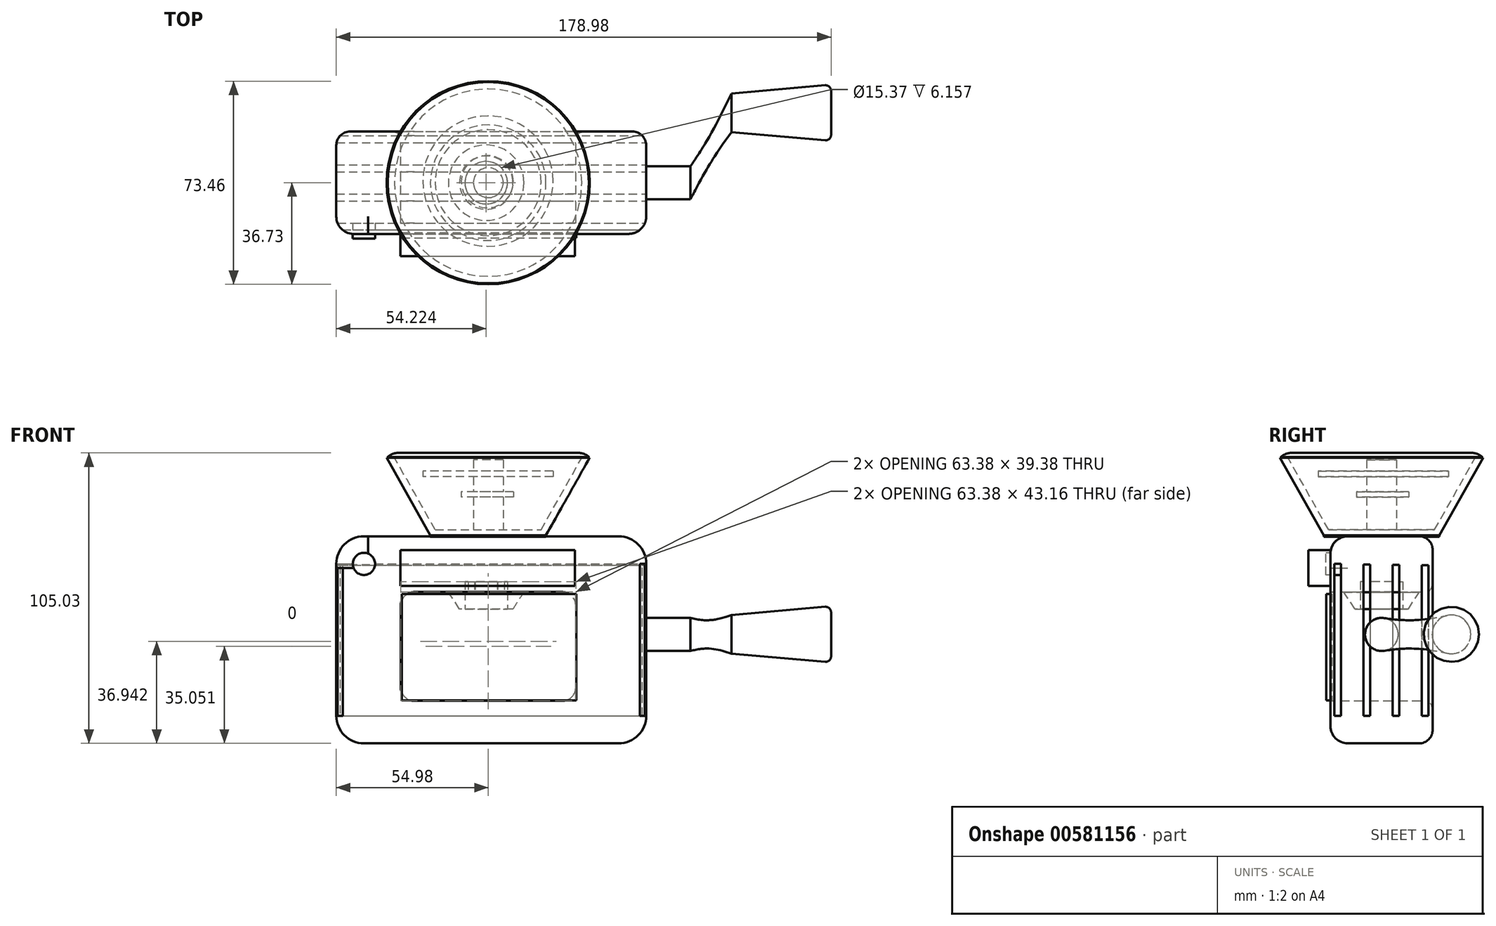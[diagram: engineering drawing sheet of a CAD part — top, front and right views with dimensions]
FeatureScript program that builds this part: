
annotation { "Feature Type Name" : "Feature", "Feature Type Description" : "" }
export const myFeature = defineFeature(function(context is Context, id is Id, definition is map)
    precondition{}
    {
        {
            var Q0;
            Q0=qCreatedBy(makeId("Front.planeOp"),FACE);
            var sketch = newSketch(context, id + "F0", { "sketchPlane" : qUnion([Q0])});
            skLineSegment(sketch, "E0.bottom", {"start": v(-54.98, 43.58) * mm, "end": v(57.14, 43.58) * mm});
            skLineSegment(sketch, "E0.top", {"start": v(-54.98, -31.33) * mm, "end": v(57.14, -31.33) * mm});
            skLineSegment(sketch, "E0.left", {"start": v(-54.98, 43.58) * mm, "end": v(-54.98, -31.33) * mm});
            skLineSegment(sketch, "E0.right", {"start": v(57.14, 43.58) * mm, "end": v(57.14, -31.33) * mm});
            skSolve(sketch);
        }
        {
            var Q0;
            Q0=makeQuery(id+"F0.imprint","IMPRINT",FACE,{"disambiguationData":[TD([[makeQuery(id+"F0.imprint","IMPRINT",EDGE,{"derivedFrom":sQuery(id+"F0.wireOp",EDGE,"E0.bottom")}),-1.0]])]});
            var sketch = newSketch(context, id + "F1", { "sketchPlane" : qUnion([Q0])});
            skLineSegment(sketch, "E1.bottom", {"start": v(-31.7, 23.4) * mm, "end": v(31.7, 23.4) * mm});
            skLineSegment(sketch, "E1.top", {"start": v(-31.7, -15.97) * mm, "end": v(31.7, -15.97) * mm});
            skLineSegment(sketch, "E1.left", {"start": v(-31.7, 23.4) * mm, "end": v(-31.7, -15.97) * mm});
            skLineSegment(sketch, "E1.right", {"start": v(31.7, 23.4) * mm, "end": v(31.7, -15.97) * mm});
            skSolve(sketch);
        }
        {
            var Q0;
            Q0=makeQuery(id+"F1.imprint","IMPRINT",FACE,{"disambiguationData":[TD([[makeQuery(id+"F1.imprint","IMPRINT",EDGE,{"derivedFrom":sQuery(id+"F1.wireOp",EDGE,"E1.bottom")}),1.0]])]});
            var sketch = newSketch(context, id + "F2", { "sketchPlane" : qUnion([Q0])});
            skSolve(sketch);
        }
        {
            var Q0;
            Q0 = qSketchRegion(id + "F2", true);
            var Q1;
            Q1=makeQuery(id+"F1.imprint","IMPRINT",FACE,{"disambiguationData":[TD([[makeQuery(id+"F1.imprint","IMPRINT",EDGE,{"derivedFrom":sQuery(id+"F1.wireOp",EDGE,"E1.bottom")}),1.0]])]});
            extrude(context, id + "F3", {"entities" : qUnion([Q0, Q1]), "endBound" : BoundingType.SYMMETRIC, "depth" : 37 * mm, "offsetDistance" : 25 * mm});
        }
        {
            var Q0;
            Q0=makeQuery(id+"F3.opExtrude","SWEPT_EDGE",EDGE,{"disambiguationData":[OSD([sQuery(id+"F0.wireOp",EDGE,"E0.bottom"),sQuery(id+"F0.wireOp",EDGE,"E0.right")])]});
            var Q1;
            Q1=makeQuery(id+"F3.opExtrude","SWEPT_EDGE",EDGE,{"disambiguationData":[OSD([sQuery(id+"F0.wireOp",EDGE,"E0.bottom"),sQuery(id+"F0.wireOp",EDGE,"E0.left")])]});
            var Q2;
            Q2=makeQuery(id+"F3.opExtrude","SWEPT_EDGE",EDGE,{"disambiguationData":[OSD([sQuery(id+"F0.wireOp",EDGE,"E0.top"),sQuery(id+"F0.wireOp",EDGE,"E0.right")])]});
            var Q3;
            Q3=makeQuery(id+"F3.opExtrude","SWEPT_EDGE",EDGE,{"disambiguationData":[OSD([sQuery(id+"F0.wireOp",EDGE,"E0.top"),sQuery(id+"F0.wireOp",EDGE,"E0.left")])]});
            fillet(context, id + "F4", {"entities" : qUnion([Q0, Q1, Q2, Q3]), "radius" : 10 * mm, "tangentPropagation" : true, "allowEdgeOverflow" : false});
        }
        {
            var Q0;
            Q0=makeQuery(id+"F3.opExtrude","SWEPT_EDGE",EDGE,{"disambiguationData":[OSD([sQuery(id+"F1.wireOp",EDGE,"E1.top"),sQuery(id+"F1.wireOp",EDGE,"E1.right")])]});
            var Q1;
            Q1=makeQuery(id+"F3.opExtrude","SWEPT_EDGE",EDGE,{"disambiguationData":[OSD([sQuery(id+"F1.wireOp",EDGE,"E1.bottom"),sQuery(id+"F1.wireOp",EDGE,"E1.right")])]});
            var Q2;
            Q2=makeQuery(id+"F3.opExtrude","SWEPT_EDGE",EDGE,{"disambiguationData":[OSD([sQuery(id+"F1.wireOp",EDGE,"E1.bottom"),sQuery(id+"F1.wireOp",EDGE,"E1.left")])]});
            var Q3;
            Q3=makeQuery(id+"F3.opExtrude","SWEPT_EDGE",EDGE,{"disambiguationData":[OSD([sQuery(id+"F1.wireOp",EDGE,"E1.top"),sQuery(id+"F1.wireOp",EDGE,"E1.left")])]});
            fillet(context, id + "F5", {"entities" : qUnion([Q0, Q1, Q2, Q3]), "radius" : 5 * mm, "tangentPropagation" : true, "allowEdgeOverflow" : false});
        }
        {
            var Q0;
            Q0=makeQuery(id+"F3.opExtrude","SWEPT_FACE",FACE,{"disambiguationData":[OSD([sQuery(id+"F0.wireOp",EDGE,"E0.right")])]});
            var sketch = newSketch(context, id + "F6", { "sketchPlane" : qUnion([Q0])});
            skLineSegment(sketch, "E2.bottom", {"start": v(-17.1, 33.58) * mm, "end": v(-14.63, 33.58) * mm});
            skLineSegment(sketch, "E2.top", {"start": v(-17.1, -21.33) * mm, "end": v(-14.63, -21.33) * mm});
            skLineSegment(sketch, "E2.left", {"start": v(-17.1, 33.58) * mm, "end": v(-17.1, -21.33) * mm});
            skLineSegment(sketch, "E2.right", {"start": v(-14.63, 33.58) * mm, "end": v(-14.63, -21.33) * mm});
            skLineSegment(sketch, "E3.1.0.0", {"start": v(-4.1, 33.4) * mm, "end": v(-4.1, -21.5) * mm});
            skLineSegment(sketch, "E3.1.0.1", {"start": v(-6.57, 33.4) * mm, "end": v(-4.1, 33.4) * mm});
            skLineSegment(sketch, "E3.1.0.2", {"start": v(-6.57, -21.5) * mm, "end": v(-4.1, -21.5) * mm});
            skLineSegment(sketch, "E3.1.0.3", {"start": v(-6.57, 33.4) * mm, "end": v(-6.57, -21.5) * mm});
            skLineSegment(sketch, "E3.2.0.0", {"start": v(6.43, 33.24) * mm, "end": v(6.43, -21.67) * mm});
            skLineSegment(sketch, "E3.2.0.1", {"start": v(3.97, 33.24) * mm, "end": v(6.43, 33.24) * mm});
            skLineSegment(sketch, "E3.2.0.2", {"start": v(3.97, -21.67) * mm, "end": v(6.43, -21.67) * mm});
            skLineSegment(sketch, "E3.2.0.3", {"start": v(3.97, 33.24) * mm, "end": v(3.97, -21.67) * mm});
            skLineSegment(sketch, "E3.3.0.0", {"start": v(16.96, 33.07) * mm, "end": v(16.96, -21.84) * mm});
            skLineSegment(sketch, "E3.3.0.1", {"start": v(14.5, 33.07) * mm, "end": v(16.96, 33.07) * mm});
            skLineSegment(sketch, "E3.3.0.2", {"start": v(14.5, -21.84) * mm, "end": v(16.96, -21.84) * mm});
            skLineSegment(sketch, "E3.3.0.3", {"start": v(14.5, 33.07) * mm, "end": v(14.5, -21.84) * mm});
            skLineSegment(sketch, "E3.direction1", {"start": v(-14.63, -21.33) * mm, "end": v(-4.1, -21.5) * mm, "construction": true});
            skSolve(sketch);
        }
        {
            var Q0;
            Q0=makeQuery(id+"F6.imprint","IMPRINT",FACE,{"disambiguationData":[TD([[makeQuery(id+"F6.imprint","IMPRINT",EDGE,{"derivedFrom":sQuery(id+"F6.wireOp",EDGE,"E2.bottom")}),1.0]])]});
            var Q1;
            {var subQ0=sQuery(id+"F6.wireOp",EDGE,"E3.1.0.1");Q1=makeQuery(id+"F6.imprint","IMPRINT",FACE,{"disambiguationData":[TD([[makeQuery(id+"F6.imprint","IMPRINT",EDGE,{"derivedFrom":subQ0}),-1.0]])]});}
            var Q2;
            {var subQ0=sQuery(id+"F6.wireOp",EDGE,"E3.2.0.1");Q2=makeQuery(id+"F6.imprint","IMPRINT",FACE,{"disambiguationData":[TD([[makeQuery(id+"F6.imprint","IMPRINT",EDGE,{"derivedFrom":subQ0}),-1.0]])]});}
            var Q3;
            {var subQ0=sQuery(id+"F6.wireOp",EDGE,"E3.3.0.1");Q3=makeQuery(id+"F6.imprint","IMPRINT",FACE,{"disambiguationData":[TD([[makeQuery(id+"F6.imprint","IMPRINT",EDGE,{"derivedFrom":subQ0}),-1.0]])]});}
            extrude(context, id + "F7", {"entities" : qUnion([Q0, Q1, Q2, Q3]), "operationType" : NewBodyOperationType.REMOVE, "oppositeDirection" : true, "depth" : 120 * mm, "offsetDistance" : 25 * mm});
        }
        {
            var Q0;
            {var subQ2=sQuery(id+"F0.wireOp",EDGE,"E0.right");var subQ7=makeQuery(id+"F3.opExtrude","SWEPT_FACE",FACE,{"disambiguationData":[OSD([subQ2])]});Q0=makeQuery(id+"F7.boolean.opBoolean","SPLIT",FACE,{"disambiguationData":[TD([makeQuery(id+"F7.opExtrude","SWEPT_FACE",FACE,{"disambiguationData":[OSD([sQuery(id+"F6.wireOp",EDGE,"E2.right")])]})])],"derivedFrom":subQ7});}
            var sketch = newSketch(context, id + "F8", { "sketchPlane" : qUnion([Q0])});
            skCircle(sketch, "E4", {"center": v(0, 8.07) * mm, "radius": 6 * mm});
            skSolve(sketch);
        }
        {
            var Q0;
            {var subQ0=sQuery(id+"F8.wireOp",EDGE,"E4");var subQ1=makeQuery(id+"F7.boolean.opBoolean","COPY",EDGE,{"derivedFrom":makeQuery(id+"F7.opExtrude","CAP_EDGE",EDGE,{"disambiguationData":[OSD([sQuery(id+"F6.wireOp",EDGE,"E3.2.0.3")])],"isStart":true})});var subQ2=makeQuery(id+"F8.imprint","INTERSECT",VERTEX,{"disambiguationData":[OD(0.0)],"derivedFrom":[subQ1,subQ0]});Q0=makeQuery(id+"F8.imprint","IMPRINT",FACE,{"disambiguationData":[TD([[makeQuery(id+"F8.imprint","IMPRINT",EDGE,{"disambiguationData":[TD([[subQ2,1.0]])],"derivedFrom":subQ0}),1.0]])]});}
            var Q1;
            {var subQ0=sQuery(id+"F8.wireOp",EDGE,"E4");var subQ1=makeQuery(id+"F7.boolean.opBoolean","COPY",EDGE,{"derivedFrom":makeQuery(id+"F7.opExtrude","CAP_EDGE",EDGE,{"disambiguationData":[OSD([sQuery(id+"F6.wireOp",EDGE,"E3.1.0.0")])],"isStart":true})});var subQ2=makeQuery(id+"F8.imprint","INTERSECT",VERTEX,{"disambiguationData":[OD(0.0)],"derivedFrom":[subQ1,subQ0]});Q1=makeQuery(id+"F8.imprint","IMPRINT",FACE,{"disambiguationData":[TD([[makeQuery(id+"F8.imprint","IMPRINT",EDGE,{"disambiguationData":[TD([[subQ2,1.0]])],"derivedFrom":subQ0}),1.0]])]});}
            var Q2;
            {var subQ0=sQuery(id+"F8.wireOp",EDGE,"E4");var subQ1=makeQuery(id+"F7.boolean.opBoolean","COPY",EDGE,{"derivedFrom":makeQuery(id+"F7.opExtrude","CAP_EDGE",EDGE,{"disambiguationData":[OSD([sQuery(id+"F6.wireOp",EDGE,"E3.1.0.0")])],"isStart":true})});var subQ2=makeQuery(id+"F8.imprint","INTERSECT",VERTEX,{"disambiguationData":[OD(0.0)],"derivedFrom":[subQ1,subQ0]});Q2=makeQuery(id+"F8.imprint","IMPRINT",FACE,{"disambiguationData":[TD([[makeQuery(id+"F8.imprint","IMPRINT",EDGE,{"disambiguationData":[TD([[subQ2,-1.0]])],"derivedFrom":subQ0}),1.0]])]});}
            extrude(context, id + "F9", {"entities" : qUnion([Q0, Q1, Q2]), "operationType" : NewBodyOperationType.ADD, "depth" : 16 * mm, "offsetDistance" : 25 * mm});
        }
        {
            var Q0;
            Q0=qCreatedBy(makeId("Right.planeOp"),FACE);
            cPlane(context, id + "F10", {"entities" : qUnion([Q0]), "cplaneType" : CPlaneType.OFFSET, "offset" : 88 * mm, "width" : 150 * mm, "height" : 150 * mm});
        }
        {
            var Q0;
            Q0=qCreatedBy(id+"F10.planeOp",FACE);
            var sketch = newSketch(context, id + "F11", { "sketchPlane" : qUnion([Q0])});
            skCircle(sketch, "E5", {"center": v(25.27, 8.1) * mm, "radius": 7 * mm});
            skSolve(sketch);
        }
        {
            var Q0;
            Q0=makeQuery(id+"F9.opExtrude","CAP_FACE",FACE,{"disambiguationData":[OSD([sQuery(id+"F8.wireOp",EDGE,"E4")])],"isStart":false});
            var sketch = newSketch(context, id + "F12", { "sketchPlane" : qUnion([Q0])});
            skCircle(sketch, "E6", {"center": v(0, 8.07) * mm, "radius": 6 * mm});
            skSolve(sketch);
        }
        {
            var Q0;
            Q0 = qSketchRegion(id + "F11", true);
            var Q1;
            Q1 = qSketchRegion(id + "F12", true);
            loft(context, id + "F13", {"sheetProfilesArray" : [{ "sheetProfileEntities" : qUnion([Q0]) }, { "sheetProfileEntities" : qUnion([Q1]) }]});
        }
        {
            var Q0;
            Q0=makeQuery(id+"F11.imprint","IMPRINT",FACE,{"disambiguationData":[TD([[makeQuery(id+"F11.imprint","IMPRINT",EDGE,{"derivedFrom":sQuery(id+"F11.wireOp",EDGE,"E5")}),1.0]])]});
            extrude(context, id + "F14", {"entities" : qUnion([Q0]), "depth" : 36 * mm, "offsetDistance" : 25 * mm, "hasDraft" : true, "draftAngle" : 5 * degree});
        }
        {
            var Q0;
            Q0=makeQuery(id+"F14.opExtrude","CAP_EDGE",EDGE,{"disambiguationData":[OSD([sQuery(id+"F11.wireOp",EDGE,"E5")])],"isStart":false});
            fillet(context, id + "F15", {"entities" : qUnion([Q0]), "radius" : 2 * mm, "tangentPropagation" : true, "allowEdgeOverflow" : false});
        }
        {
            var Q0;
            Q0=qCreatedBy(makeId("Front.planeOp"),FACE);
            var sketch = newSketch(context, id + "F16", { "sketchPlane" : qUnion([Q0])});
            skLineSegment(sketch, "E7", {"start": v(-0.76, 23.3) * mm, "end": v(-0.76, 17.2) * mm});
            skLineSegment(sketch, "E8", {"start": v(-0.76, 17.2) * mm, "end": v(8.9, 17.2) * mm});
            skLineSegment(sketch, "E9", {"start": v(12.89, 23.39) * mm, "end": v(-0.76, 23.3) * mm});
            skLineSegment(sketch, "E10", {"start": v(8.9, 17.2) * mm, "end": v(12.89, 23.39) * mm});
            skSolve(sketch);
        }
        {
            var Q0;
            Q0 = qSketchRegion(id + "F16", true);
            var Q1;
            Q1=sQuery(id+"F16.wireOp",EDGE,"E7");
            revolve(context, id + "F17", {"entities" : qUnion([Q0]), "axis" : qUnion([Q1]), "revolveType" : RevolveType.FULL});
        }
        {
            var Q0;
            Q0=makeQuery(id+"F17.opRevolve","SWEPT_FACE",FACE,{"disambiguationData":[OSD([sQuery(id+"F16.wireOp",EDGE,"E8")])]});
            var sketch = newSketch(context, id + "F18", { "sketchPlane" : qUnion([Q0])});
            skCircle(sketch, "E11", {"center": v(-0.76, 0) * mm, "radius": 7.68 * mm});
            skSolve(sketch);
        }
        {
            var Q0;
            Q0 = qSketchRegion(id + "F18", true);
            extrude(context, id + "F19", {"entities" : qUnion([Q0]), "operationType" : NewBodyOperationType.REMOVE, "oppositeDirection" : true, "depth" : 10 * mm, "offsetDistance" : 25 * mm});
        }
        {
            var Q0;
            Q0=qCreatedBy(makeId("Front.planeOp"),FACE);
            var sketch = newSketch(context, id + "F20", { "sketchPlane" : qUnion([Q0])});
            skLineSegment(sketch, "E12", {"start": v(-20.93, 43.9) * mm, "end": v(-36.78, 71.99) * mm});
            skLineSegment(sketch, "E13", {"start": v(-36.78, 71.99) * mm, "end": v(-0.05, 71.99) * mm});
            skLineSegment(sketch, "E14", {"start": v(-20.93, 43.9) * mm, "end": v(-20.93, 43.4) * mm});
            skLineSegment(sketch, "E15", {"start": v(-20.93, 43.4) * mm, "end": v(-0.05, 43.4) * mm});
            skPoint(sketch, "E16.end.orphan", {"position": v(-0.34, 43.9) * mm});
            skLineSegment(sketch, "E17", {"start": v(-0.05, 71.99) * mm, "end": v(-0.05, 43.4) * mm});
            skSolve(sketch);
        }
        {
            var Q0;
            Q0=makeQuery(id+"F20.imprint","IMPRINT",FACE,{"disambiguationData":[TD([[makeQuery(id+"F20.imprint","IMPRINT",EDGE,{"derivedFrom":sQuery(id+"F20.wireOp",EDGE,"E12")}),-1.0]])]});
            var Q1;
            Q1=sQuery(id+"F20.wireOp",EDGE,"E17");
            revolve(context, id + "F21", {"entities" : qUnion([Q0]), "axis" : qUnion([Q1]), "revolveType" : RevolveType.FULL});
        }
        {
            var Q0;
            Q0=makeQuery(id+"F21.opRevolve","SWEPT_FACE",FACE,{"disambiguationData":[OSD([sQuery(id+"F20.wireOp",EDGE,"E13")])]});
            var sketch = newSketch(context, id + "F22", { "sketchPlane" : qUnion([Q0])});
            skCircle(sketch, "E18.cCircle", {"center": v(-0.05, 0) * mm, "radius": 17.43 * mm, "construction": true});
            skLineSegment(sketch, "E18.0", {"start": v(20.08, -0.46) * mm, "end": v(9.62, -17.66) * mm});
            skLineSegment(sketch, "E18.1", {"start": v(9.62, -17.66) * mm, "end": v(-10.5, -17.2) * mm});
            skLineSegment(sketch, "E18.2", {"start": v(-10.5, -17.2) * mm, "end": v(-20.17, 0.46) * mm});
            skLineSegment(sketch, "E18.3", {"start": v(-20.17, 0.46) * mm, "end": v(-9.7, 17.66) * mm});
            skLineSegment(sketch, "E18.4", {"start": v(-9.7, 17.66) * mm, "end": v(10.41, 17.2) * mm});
            skLineSegment(sketch, "E18.5", {"start": v(10.41, 17.2) * mm, "end": v(20.08, -0.46) * mm});
            skPoint(sketch, "E18.0.midPoint", {"position": v(14.85, -9.06) * mm});
            skSolve(sketch);
        }
        {
            var Q0;
            Q0=makeQuery(id+"F21.opRevolve","SWEPT_FACE",FACE,{"disambiguationData":[OSD([sQuery(id+"F20.wireOp",EDGE,"E13")])]});
            shell(context, id + "F23", {"entities" : qUnion([Q0]), "thickness" : 2.5 * mm});
        }
        {
            var Q0;
            Q0=qCreatedBy(makeId("Front.planeOp"),FACE);
            cPlane(context, id + "F24", {"entities" : qUnion([Q0]), "cplaneType" : CPlaneType.OFFSET, "offset" : 18 * mm, "width" : 150 * mm, "height" : 150 * mm});
        }
        {
            var Q0;
            Q0=makeQuery(id+"F3.opExtrude","CAP_FACE",FACE,{"disambiguationData":[OSD([sQuery(id+"F0.wireOp",EDGE,"E0.bottom"),sQuery(id+"F0.wireOp",EDGE,"E0.top"),sQuery(id+"F0.wireOp",EDGE,"E0.left"),sQuery(id+"F0.wireOp",EDGE,"E0.right"),sQuery(id+"F1.wireOp",EDGE,"E1.bottom"),sQuery(id+"F1.wireOp",EDGE,"E1.top"),sQuery(id+"F1.wireOp",EDGE,"E1.left"),sQuery(id+"F1.wireOp",EDGE,"E1.right")])],"isStart":false});
            var sketch = newSketch(context, id + "F25", { "sketchPlane" : qUnion([Q0])});
            skCircle(sketch, "E19", {"center": v(-44.98, 33.58) * mm, "radius": 4.02 * mm});
            skSolve(sketch);
        }
        {
            var Q0;
            Q0=makeQuery(id+"F25.imprint","IMPRINT",FACE,{"disambiguationData":[TD([[makeQuery(id+"F25.imprint","IMPRINT",EDGE,{"derivedFrom":sQuery(id+"F25.wireOp",EDGE,"E19")}),1.0]])]});
            var Q1;
            Q1=sQuery(id+"F25.wireOp",EDGE,"E19");
            extrude(context, id + "F26", {"entities" : qUnion([Q0]), "operationType" : NewBodyOperationType.ADD, "surfaceEntities" : qUnion([Q1]), "oppositeDirection" : true, "depth" : 6.1 * mm, "offsetDistance" : 25 * mm, "hasSecondDirection" : true, "secondDirectionOppositeDirection" : false, "secondDirectionDepth" : 1.7 * mm});
        }
        {
            var Q0;
            Q0=qCreatedBy(makeId("Top.planeOp"),FACE);
            cPlane(context, id + "F27", {"entities" : qUnion([Q0]), "cplaneType" : CPlaneType.OFFSET, "offset" : 44.1 * mm, "width" : 150 * mm, "height" : 150 * mm});
        }
        {
            var Q0;
            Q0=makeQuery(id+"F23.opShell","OFFSET_FACE",FACE,{"disambiguationData":[OSD([sQuery(id+"F20.wireOp",EDGE,"E15")])]});
            var sketch = newSketch(context, id + "F28", { "sketchPlane" : qUnion([Q0])});
            skCircle(sketch, "E20", {"center": v(0, 0) * mm, "radius": 5.4 * mm});
            skSolve(sketch);
        }
        {
            var Q0;
            Q0=makeQuery(id+"F28.imprint","IMPRINT",FACE,{"disambiguationData":[TD([[makeQuery(id+"F28.imprint","IMPRINT",EDGE,{"derivedFrom":sQuery(id+"F28.wireOp",EDGE,"E20")}),1.0]])]});
            extrude(context, id + "F29", {"entities" : qUnion([Q0]), "operationType" : NewBodyOperationType.ADD, "depth" : 25.3 * mm, "offsetDistance" : 25 * mm});
        }
        {
            var Q0;
            Q0=qCreatedBy(id+"F27.planeOp",FACE);
            cPlane(context, id + "F30", {"entities" : qUnion([Q0]), "cplaneType" : CPlaneType.OFFSET, "offset" : 28.1 * mm, "width" : 150 * mm, "height" : 150 * mm});
        }
        {
            var Q0;
            Q0=qCreatedBy(id+"F30.planeOp",FACE);
            var sketch = newSketch(context, id + "F31", { "sketchPlane" : qUnion([Q0])});
            skCircle(sketch, "E21", {"center": v(0, 0) * mm, "radius": 36.39 * mm});
            skSolve(sketch);
        }
        {
            var Q0;
            Q0=makeQuery(id+"F31.imprint","IMPRINT",FACE,{"disambiguationData":[TD([[makeQuery(id+"F31.imprint","IMPRINT",EDGE,{"derivedFrom":sQuery(id+"F31.wireOp",EDGE,"E21")}),1.0]])]});
            extrude(context, id + "F32", {"entities" : qUnion([Q0]), "depth" : 1.5 * mm, "offsetDistance" : 25 * mm});
        }
        {
            var Q0;
            Q0=makeQuery(id+"F3.opExtrude","CAP_FACE",FACE,{"disambiguationData":[OSD([sQuery(id+"F0.wireOp",EDGE,"E0.bottom"),sQuery(id+"F0.wireOp",EDGE,"E0.top"),sQuery(id+"F0.wireOp",EDGE,"E0.left"),sQuery(id+"F0.wireOp",EDGE,"E0.right"),sQuery(id+"F1.wireOp",EDGE,"E1.bottom"),sQuery(id+"F1.wireOp",EDGE,"E1.top"),sQuery(id+"F1.wireOp",EDGE,"E1.left"),sQuery(id+"F1.wireOp",EDGE,"E1.right")])],"isStart":false});
            var sketch = newSketch(context, id + "F33", { "sketchPlane" : qUnion([Q0])});
            skLineSegment(sketch, "E22.bottom", {"start": v(-31.8, 38.53) * mm, "end": v(31.34, 38.53) * mm});
            skLineSegment(sketch, "E22.top", {"start": v(-31.8, 25.57) * mm, "end": v(31.34, 25.57) * mm});
            skLineSegment(sketch, "E22.left", {"start": v(-31.8, 38.53) * mm, "end": v(-31.8, 25.57) * mm});
            skLineSegment(sketch, "E22.right", {"start": v(31.34, 38.53) * mm, "end": v(31.34, 25.57) * mm});
            skSolve(sketch);
        }
        {
            var Q0;
            Q0=makeQuery(id+"F33.imprint","IMPRINT",FACE,{"disambiguationData":[TD([[makeQuery(id+"F33.imprint","IMPRINT",EDGE,{"derivedFrom":sQuery(id+"F33.wireOp",EDGE,"E22.bottom")}),-1.0]])]});
            extrude(context, id + "F34", {"entities" : qUnion([Q0]), "operationType" : NewBodyOperationType.ADD, "depth" : 8 * mm, "offsetDistance" : 25 * mm});
        }
        {
            var Q0;
            {var subQ0=sQuery(id+"F0.wireOp",EDGE,"E0.right");var subQ1=sQuery(id+"F0.wireOp",EDGE,"E0.bottom");Q0=makeQuery(id+"F4.opFillet","BLEND_EDGE",EDGE,{"blendedFrom":[makeQuery(id+"F3.opExtrude","SWEPT_EDGE",EDGE,{"disambiguationData":[OSD([subQ1,subQ0])]}),makeQuery(id+"F3.opExtrude","CAP_FACE",FACE,{"disambiguationData":[OSD([subQ1,sQuery(id+"F0.wireOp",EDGE,"E0.top"),sQuery(id+"F0.wireOp",EDGE,"E0.left"),subQ0,sQuery(id+"F1.wireOp",EDGE,"E1.bottom"),sQuery(id+"F1.wireOp",EDGE,"E1.top"),sQuery(id+"F1.wireOp",EDGE,"E1.left"),sQuery(id+"F1.wireOp",EDGE,"E1.right")])],"isStart":false})],"blendedInto":[makeQuery(id+"F3.opExtrude","CAP_FACE",FACE,{"disambiguationData":[OSD([subQ1,sQuery(id+"F0.wireOp",EDGE,"E0.top"),sQuery(id+"F0.wireOp",EDGE,"E0.left"),subQ0,sQuery(id+"F1.wireOp",EDGE,"E1.bottom"),sQuery(id+"F1.wireOp",EDGE,"E1.top"),sQuery(id+"F1.wireOp",EDGE,"E1.left"),sQuery(id+"F1.wireOp",EDGE,"E1.right")])],"isStart":false})]});}
            fillet(context, id + "F35", {"entities" : qUnion([Q0]), "radius" : 6.28 * mm, "tangentPropagation" : true, "allowEdgeOverflow" : false});
        }
        {
            var Q0;
            Q0=makeQuery(id+"F3.opExtrude","CAP_EDGE",EDGE,{"disambiguationData":[OSD([sQuery(id+"F0.wireOp",EDGE,"E0.bottom")])],"isStart":true});
            var Q1;
            Q1=makeQuery(id+"F3.opExtrude","CAP_EDGE",EDGE,{"disambiguationData":[OSD([sQuery(id+"F0.wireOp",EDGE,"E0.right")])],"isStart":true});
            var Q2;
            {var subQ0=sQuery(id+"F0.wireOp",EDGE,"E0.right");var subQ1=sQuery(id+"F0.wireOp",EDGE,"E0.bottom");Q2=makeQuery(id+"F4.opFillet","BLEND_EDGE",EDGE,{"blendedFrom":[makeQuery(id+"F3.opExtrude","SWEPT_EDGE",EDGE,{"disambiguationData":[OSD([subQ1,subQ0])]}),makeQuery(id+"F3.opExtrude","CAP_FACE",FACE,{"disambiguationData":[OSD([subQ1,sQuery(id+"F0.wireOp",EDGE,"E0.top"),sQuery(id+"F0.wireOp",EDGE,"E0.left"),subQ0,sQuery(id+"F1.wireOp",EDGE,"E1.bottom"),sQuery(id+"F1.wireOp",EDGE,"E1.top"),sQuery(id+"F1.wireOp",EDGE,"E1.left"),sQuery(id+"F1.wireOp",EDGE,"E1.right")])],"isStart":true})],"blendedInto":[makeQuery(id+"F3.opExtrude","CAP_FACE",FACE,{"disambiguationData":[OSD([subQ1,sQuery(id+"F0.wireOp",EDGE,"E0.top"),sQuery(id+"F0.wireOp",EDGE,"E0.left"),subQ0,sQuery(id+"F1.wireOp",EDGE,"E1.bottom"),sQuery(id+"F1.wireOp",EDGE,"E1.top"),sQuery(id+"F1.wireOp",EDGE,"E1.left"),sQuery(id+"F1.wireOp",EDGE,"E1.right")])],"isStart":true})]});}
            fillet(context, id + "F36", {"entities" : qUnion([Q0, Q1, Q2]), "radius" : 5 * mm, "tangentPropagation" : true, "allowEdgeOverflow" : false});
        }
        {
            var Q0;
            Q0=makeQuery(id+"F32.opExtrude","CAP_EDGE",EDGE,{"disambiguationData":[OSD([sQuery(id+"F31.wireOp",EDGE,"E21")])],"isStart":false});
            fillet(context, id + "F37", {"entities" : qUnion([Q0]), "radius" : 5 * mm, "tangentPropagation" : true, "allowEdgeOverflow" : false});
        }
        {
            var Q0;
            Q0=makeQuery(id+"F3.opExtrude","CAP_EDGE",EDGE,{"disambiguationData":[OSD([sQuery(id+"F1.wireOp",EDGE,"E1.right")])],"isStart":true});
            fillet(context, id + "F38", {"entities" : qUnion([Q0]), "radius" : 5 * mm, "tangentPropagation" : true, "allowEdgeOverflow" : false});
        }
        {
            var Q0;
            Q0=qCreatedBy(id+"F24.planeOp",FACE);
            var sketch = newSketch(context, id + "F39", { "sketchPlane" : qUnion([Q0])});
            skLineSegment(sketch, "E23.bottom", {"start": v(-31.32, 22.69) * mm, "end": v(31.82, 22.69) * mm});
            skLineSegment(sketch, "E23.top", {"start": v(-31.32, -15.73) * mm, "end": v(31.82, -15.73) * mm});
            skLineSegment(sketch, "E23.left", {"start": v(-31.32, 22.69) * mm, "end": v(-31.32, -15.73) * mm});
            skLineSegment(sketch, "E23.right", {"start": v(31.82, 22.69) * mm, "end": v(31.82, -15.73) * mm});
            skSolve(sketch);
        }
        {
            var Q0;
            Q0=makeQuery(id+"F39.imprint","IMPRINT",FACE,{"disambiguationData":[TD([[makeQuery(id+"F39.imprint","IMPRINT",EDGE,{"derivedFrom":sQuery(id+"F39.wireOp",EDGE,"E23.bottom")}),-1.0]])]});
            extrude(context, id + "F40", {"entities" : qUnion([Q0]), "depth" : 2 * mm, "offsetDistance" : 25 * mm});
        }
        {
            var Q0;
            Q0=qCreatedBy(id+"F30.planeOp",FACE);
            cPlane(context, id + "F41", {"entities" : qUnion([Q0]), "cplaneType" : CPlaneType.OFFSET, "offset" : 14.5 * mm, "oppositeDirection" : true, "width" : 150 * mm, "height" : 150 * mm});
        }
        {
            var Q0;
            Q0=qCreatedBy(id+"F41.planeOp",FACE);
            var sketch = newSketch(context, id + "F42", { "sketchPlane" : qUnion([Q0])});
            skCircle(sketch, "E24", {"center": v(-0.35, 0.36) * mm, "radius": 9.44 * mm});
            skSolve(sketch);
        }
        {
            var Q0;
            Q0=makeQuery(id+"F42.imprint","IMPRINT",FACE,{"disambiguationData":[TD([[makeQuery(id+"F42.imprint","IMPRINT",EDGE,{"derivedFrom":sQuery(id+"F42.wireOp",EDGE,"E24")}),1.0]])]});
            extrude(context, id + "F43", {"entities" : qUnion([Q0]), "operationType" : NewBodyOperationType.ADD, "depth" : 2 * mm, "offsetDistance" : 25 * mm});
        }
        {
            var Q0;
            Q0=qCreatedBy(id+"F41.planeOp",FACE);
            cPlane(context, id + "F44", {"entities" : qUnion([Q0]), "cplaneType" : CPlaneType.OFFSET, "offset" : 10.8 * mm, "width" : 150 * mm, "height" : 150 * mm});
        }
        {
            var Q0;
            Q0=qCreatedBy(id+"F44.planeOp",FACE);
            cPlane(context, id + "F45", {"entities" : qUnion([Q0]), "cplaneType" : CPlaneType.OFFSET, "offset" : 3.4 * mm, "oppositeDirection" : true, "width" : 150 * mm, "height" : 150 * mm});
        }
        {
            var Q0;
            Q0=qCreatedBy(id+"F45.planeOp",FACE);
            var sketch = newSketch(context, id + "F46", { "sketchPlane" : qUnion([Q0])});
            skCircle(sketch, "E25", {"center": v(-0.1, 0.6) * mm, "radius": 23.55 * mm});
            skSolve(sketch);
        }
        {
            var Q0;
            Q0=makeQuery(id+"F46.imprint","IMPRINT",FACE,{"disambiguationData":[TD([[makeQuery(id+"F46.imprint","IMPRINT",EDGE,{"derivedFrom":sQuery(id+"F46.wireOp",EDGE,"E25")}),1.0]])]});
            extrude(context, id + "F47", {"entities" : qUnion([Q0]), "operationType" : NewBodyOperationType.ADD, "depth" : 2 * mm, "offsetDistance" : 25 * mm});
        }
    });
